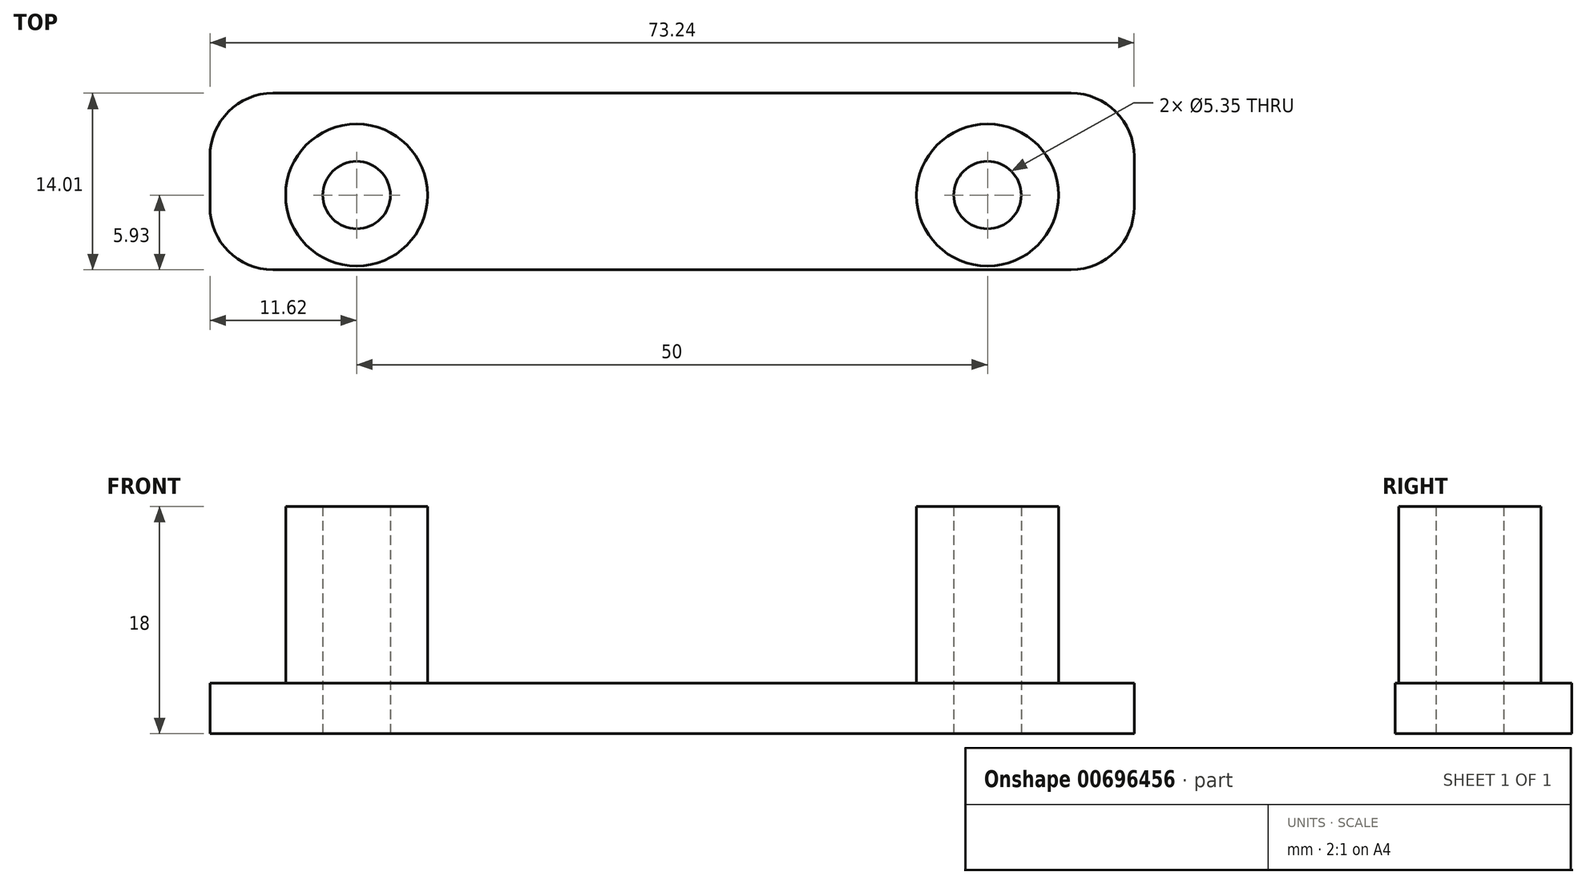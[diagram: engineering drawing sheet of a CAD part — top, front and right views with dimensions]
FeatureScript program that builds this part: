
annotation { "Feature Type Name" : "Feature", "Feature Type Description" : "" }
export const myFeature = defineFeature(function(context is Context, id is Id, definition is map)
    precondition{}
    {
        {
            var Q0;
            Q0=qCreatedBy(makeId("Top.planeOp"),FACE);
            var sketch = newSketch(context, id + "F0", { "sketchPlane" : qUnion([Q0])});
            skCircle(sketch, "E0", {"center": v(-25, 0) * mm, "radius": 5.62 * mm});
            skCircle(sketch, "E1", {"center": v(25, 0) * mm, "radius": 5.62 * mm});
            skCircle(sketch, "E2", {"center": v(-25, 0) * mm, "radius": 2.67 * mm});
            skCircle(sketch, "E3", {"center": v(25, 0) * mm, "radius": 2.67 * mm});
            skLineSegment(sketch, "E4.bottom", {"start": v(-31.63, 8.08) * mm, "end": v(31.63, 8.08) * mm});
            skLineSegment(sketch, "E4.top", {"start": v(-31.63, -5.92) * mm, "end": v(31.63, -5.92) * mm});
            skLineSegment(sketch, "E4.left", {"start": v(-36.63, 3.08) * mm, "end": v(-36.63, -0.92) * mm});
            skLineSegment(sketch, "E4.right", {"start": v(36.63, 3.08) * mm, "end": v(36.63, -0.92) * mm});
            skPoint(sketch, "E5.visualSharp", {"position": v(-36.63, 8.08) * mm});
            skArc(sketch, "E5.filletArc", {"start": v(-31.63, 8.07) * mm, "mid": v(-35.16, 6.61) * mm, "end": v(-36.63, 3.08) * mm});
            skPoint(sketch, "E6.visualSharp", {"position": v(-36.63, -5.92) * mm});
            skArc(sketch, "E6.filletArc", {"start": v(-36.63, -0.93) * mm, "mid": v(-35.16, -4.46) * mm, "end": v(-31.63, -5.92) * mm});
            skPoint(sketch, "E7.visualSharp", {"position": v(36.63, -5.92) * mm});
            skArc(sketch, "E7.filletArc", {"start": v(31.63, -5.93) * mm, "mid": v(35.16, -4.46) * mm, "end": v(36.63, -0.92) * mm});
            skPoint(sketch, "E8.visualSharp", {"position": v(36.63, 8.08) * mm});
            skArc(sketch, "E8.filletArc", {"start": v(36.63, 3.08) * mm, "mid": v(35.16, 6.61) * mm, "end": v(31.63, 8.08) * mm});
            skSolve(sketch);
        }
        {
            var Q0;
            Q0=makeQuery(id+"F0.imprint","IMPRINT",FACE,{"disambiguationData":[TD([[makeQuery(id+"F0.imprint","IMPRINT",EDGE,{"derivedFrom":sQuery(id+"F0.wireOp",EDGE,"E0")}),1.0]])]});
            var Q1;
            Q1=makeQuery(id+"F0.imprint","IMPRINT",FACE,{"disambiguationData":[TD([[makeQuery(id+"F0.imprint","IMPRINT",EDGE,{"derivedFrom":sQuery(id+"F0.wireOp",EDGE,"E1")}),1.0]])]});
            extrude(context, id + "F1", {"entities" : qUnion([Q0, Q1]), "depth" : 14 * mm, "offsetDistance" : 25 * mm});
        }
        {
            var Q0;
            Q0=makeQuery(id+"F0.imprint","IMPRINT",FACE,{"disambiguationData":[TD([[makeQuery(id+"F0.imprint","IMPRINT",EDGE,{"derivedFrom":sQuery(id+"F0.wireOp",EDGE,"E0")}),-1.0]])]});
            var Q1;
            Q1=makeQuery(id+"F0.imprint","IMPRINT",FACE,{"disambiguationData":[TD([[makeQuery(id+"F0.imprint","IMPRINT",EDGE,{"derivedFrom":sQuery(id+"F0.wireOp",EDGE,"E0")}),1.0]])]});
            var Q2;
            Q2=makeQuery(id+"F0.imprint","IMPRINT",FACE,{"disambiguationData":[TD([[makeQuery(id+"F0.imprint","IMPRINT",EDGE,{"derivedFrom":sQuery(id+"F0.wireOp",EDGE,"E1")}),1.0]])]});
            extrude(context, id + "F2", {"entities" : qUnion([Q0, Q1, Q2]), "operationType" : NewBodyOperationType.ADD, "oppositeDirection" : true, "depth" : 4 * mm, "offsetDistance" : 25 * mm});
        }
    });
